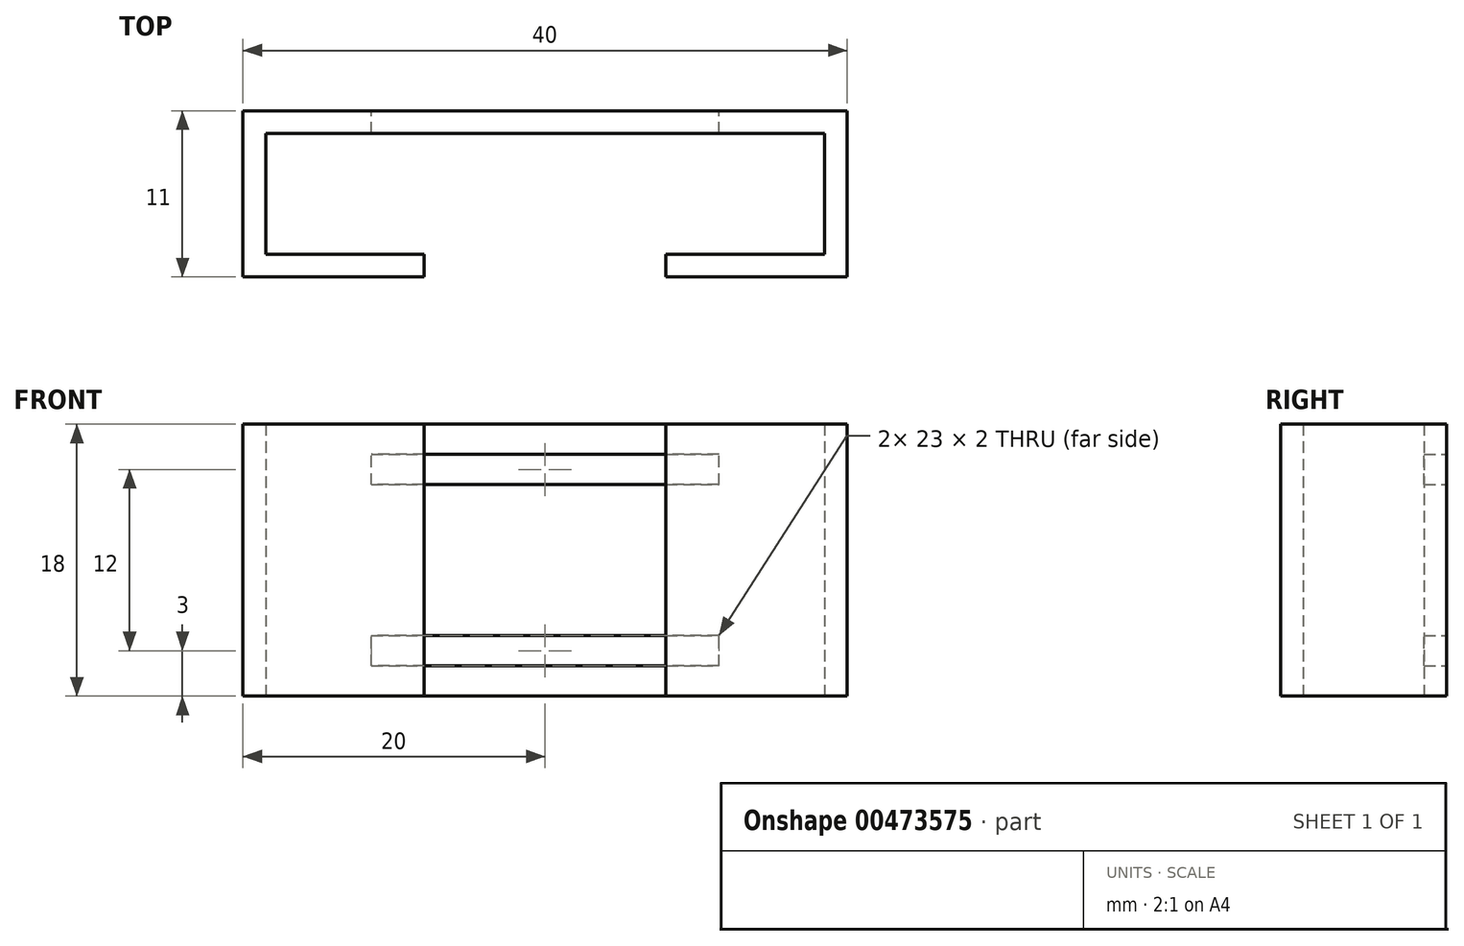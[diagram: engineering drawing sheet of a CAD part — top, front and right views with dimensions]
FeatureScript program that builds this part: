
annotation { "Feature Type Name" : "Feature", "Feature Type Description" : "" }
export const myFeature = defineFeature(function(context is Context, id is Id, definition is map)
    precondition{}
    {
        {
            var Q0;
            Q0=qCreatedBy(makeId("Top.planeOp"),FACE);
            var sketch = newSketch(context, id + "F0", { "sketchPlane" : qUnion([Q0])});
            skLineSegment(sketch, "E0.bottom", {"start": v(18.5, 4) * mm, "end": v(-18.5, 4) * mm});
            skLineSegment(sketch, "E0.top", {"start": v(18.5, -4) * mm, "end": v(-18.5, -4) * mm});
            skLineSegment(sketch, "E0.left", {"start": v(18.5, 4) * mm, "end": v(18.5, -4) * mm});
            skLineSegment(sketch, "E0.right", {"start": v(-18.5, 4) * mm, "end": v(-18.5, -4) * mm});
            skPoint(sketch, "E0.middle", {"position": v(0, 0) * mm});
            skLineSegment(sketch, "E1.bottom", {"start": v(20, 5.5) * mm, "end": v(-20, 5.5) * mm});
            skLineSegment(sketch, "E1.top", {"start": v(20, -5.5) * mm, "end": v(-20, -5.5) * mm});
            skLineSegment(sketch, "E1.left", {"start": v(20, 5.5) * mm, "end": v(20, -5.5) * mm});
            skLineSegment(sketch, "E1.right", {"start": v(-20, 5.5) * mm, "end": v(-20, -5.5) * mm});
            skLineSegment(sketch, "E2.bottom", {"start": v(-8, -4) * mm, "end": v(8, -4) * mm});
            skLineSegment(sketch, "E2.top", {"start": v(-8, -5.5) * mm, "end": v(8, -5.5) * mm});
            skLineSegment(sketch, "E2.left", {"start": v(-8, -4) * mm, "end": v(-8, -5.5) * mm});
            skLineSegment(sketch, "E2.right", {"start": v(8, -4) * mm, "end": v(8, -5.5) * mm});
            skSolve(sketch);
        }
        {
            var Q0;
            Q0=makeQuery(id+"F0.imprint","IMPRINT",FACE,{"disambiguationData":[TD([[makeQuery(id+"F0.imprint","IMPRINT",EDGE,{"derivedFrom":sQuery(id+"F0.wireOp",EDGE,"E0.bottom")}),-1.0]])]});
            extrude(context, id + "F1", {"entities" : qUnion([Q0]), "depth" : 18 * mm});
        }
        {
            var Q0;
            Q0=makeQuery(id+"F1.opExtrude","SWEPT_FACE",FACE,{"disambiguationData":[OSD([sQuery(id+"F0.wireOp",EDGE,"E1.bottom")])]});
            var sketch = newSketch(context, id + "F2", { "sketchPlane" : qUnion([Q0])});
            skPoint(sketch, "E3", {"position": v(0, 9) * mm});
            skLineSegment(sketch, "E4.bottom", {"start": v(11.5, 16) * mm, "end": v(-11.5, 16) * mm});
            skLineSegment(sketch, "E4.top", {"start": v(11.5, 2) * mm, "end": v(-11.5, 2) * mm});
            skLineSegment(sketch, "E4.left", {"start": v(11.5, 16) * mm, "end": v(11.5, 2) * mm});
            skLineSegment(sketch, "E4.right", {"start": v(-11.5, 16) * mm, "end": v(-11.5, 2) * mm});
            skLineSegment(sketch, "E5", {"start": v(-11.5, 14) * mm, "end": v(11.5, 14) * mm});
            skLineSegment(sketch, "E6", {"start": v(-11.5, 4) * mm, "end": v(11.5, 4) * mm});
            skSolve(sketch);
        }
        {
            var Q0;
            {var subQ0=sQuery(id+"F2.wireOp",EDGE,"E4.bottom");Q0=makeQuery(id+"F2.imprint","IMPRINT",FACE,{"disambiguationData":[TD([[makeQuery(id+"F2.imprint","IMPRINT",EDGE,{"derivedFrom":subQ0}),1.0]])]});}
            var Q1;
            {var subQ0=sQuery(id+"F2.wireOp",EDGE,"E4.top");Q1=makeQuery(id+"F2.imprint","IMPRINT",FACE,{"disambiguationData":[TD([[makeQuery(id+"F2.imprint","IMPRINT",EDGE,{"derivedFrom":subQ0}),-1.0]])]});}
            extrude(context, id + "F3", {"entities" : qUnion([Q0, Q1]), "operationType" : NewBodyOperationType.REMOVE, "oppositeDirection" : true, "depth" : 2 * mm});
        }
    });
